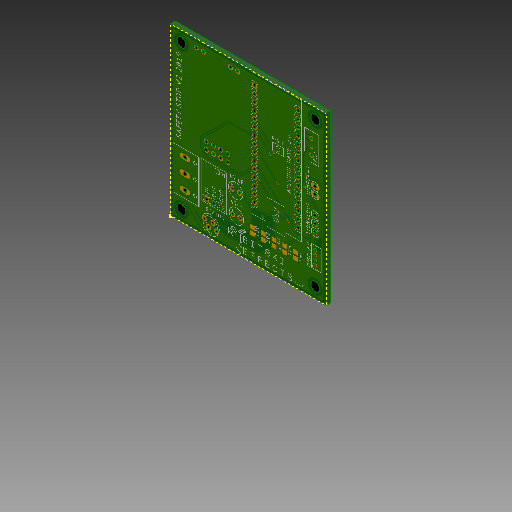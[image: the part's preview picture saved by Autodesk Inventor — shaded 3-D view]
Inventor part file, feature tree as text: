
AUTODESK INVENTOR PART (.ipt)
format: ipt  version: 2019 (Build 230136000, 136)  size: 475,648 bytes
history: native  units: in
note: dims shown in document units (in); Inventor stores cm internally (conversion verified against a paired STEP export)
features: sketch x3, other x2
ambient origin geometry x8: Origin, YZ Plane, XZ Plane, XY Plane, X Axis, Y Axis, Z Axis, Center Point
bodies: Solid1 (feature_tree)
feature tree (5):
  other  "estop v2.brd_Outline"
  sketch  "Sketch2"
  sketch  "Sketch3"
  sketch  "Sketch1"  dims[d0=0.0645in d1=0.0in]
  other  "Image1"
